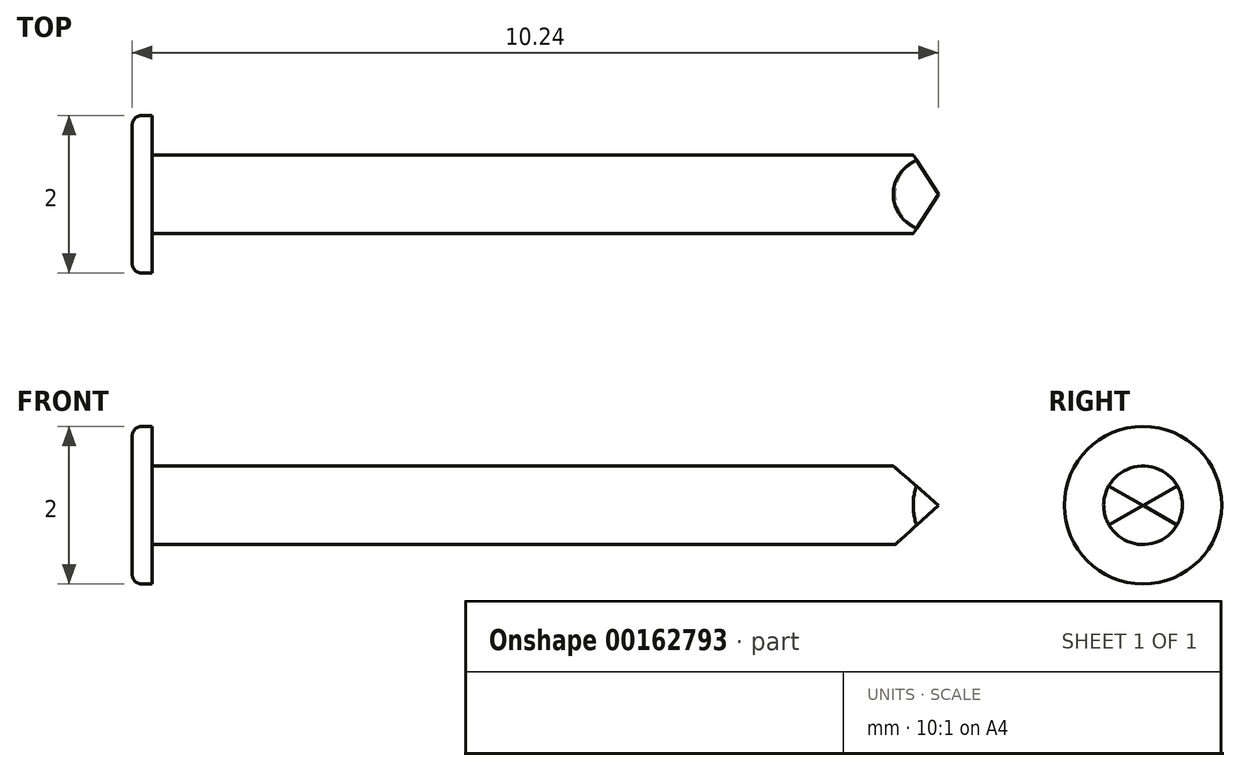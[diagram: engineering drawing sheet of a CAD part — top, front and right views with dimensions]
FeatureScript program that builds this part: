
annotation { "Feature Type Name" : "Feature", "Feature Type Description" : "" }
export const myFeature = defineFeature(function(context is Context, id is Id, definition is map)
    precondition{}
    {
        {
            var Q0;
            Q0=qCreatedBy(makeId("Right.planeOp"),FACE);
            var sketch = newSketch(context, id + "F0", { "sketchPlane" : qUnion([Q0])});
            skCircle(sketch, "E0", {"center": v(0, 0) * mm, "radius": 1 * mm});
            skCircle(sketch, "E1", {"center": v(0, 0) * mm, "radius": 0.5 * mm});
            skSolve(sketch);
        }
        {
            var Q0;
            Q0=makeQuery(id+"F0.imprint","IMPRINT",FACE,{"disambiguationData":[TD([[makeQuery(id+"F0.imprint","IMPRINT",EDGE,{"derivedFrom":sQuery(id+"F0.wireOp",EDGE,"E1")}),1.0]])]});
            var Q1;
            Q1=sQuery(id+"F0.wireOp",EDGE,"E1");
            extrude(context, id + "F1", {"entities" : qUnion([Q0]), "surfaceEntities" : qUnion([Q1]), "depth" : 10 * mm});
        }
        {
            var Q0;
            Q0=makeQuery(id+"F0.imprint","IMPRINT",FACE,{"disambiguationData":[TD([[makeQuery(id+"F0.imprint","IMPRINT",EDGE,{"derivedFrom":sQuery(id+"F0.wireOp",EDGE,"E1")}),1.0]])]});
            var Q1;
            Q1=makeQuery(id+"F0.imprint","IMPRINT",FACE,{"disambiguationData":[TD([[makeQuery(id+"F0.imprint","IMPRINT",EDGE,{"derivedFrom":sQuery(id+"F0.wireOp",EDGE,"E0")}),1.0]])]});
            var Q2;
            Q2=sQuery(id+"F0.wireOp",EDGE,"E1");
            var Q3;
            Q3=sQuery(id+"F0.wireOp",EDGE,"E0");
            extrude(context, id + "F2", {"entities" : qUnion([Q0, Q1]), "operationType" : NewBodyOperationType.ADD, "surfaceEntities" : qUnion([Q2, Q3]), "oppositeDirection" : true, "depth" : 0.25 * mm});
        }
        {
            var Q0;
            Q0=makeQuery(id+"F2.opExtrude","CAP_EDGE",EDGE,{"disambiguationData":[OSD([sQuery(id+"F0.wireOp",EDGE,"E0")])],"isStart":false});
            fillet(context, id + "F3", {"entities" : qUnion([Q0]), "radius" : 0.12 * mm, "tangentPropagation" : true, "allowEdgeOverflow" : false});
        }
        {
            var Q0;
            Q0=qCreatedBy(makeId("Front.planeOp"),FACE);
            var sketch = newSketch(context, id + "F4", { "sketchPlane" : qUnion([Q0])});
            skLineSegment(sketch, "E2", {"start": v(10, 0) * mm, "end": v(9.12, -0.8) * mm});
            skLineSegment(sketch, "E3", {"start": v(9.12, -0.8) * mm, "end": v(10.61, -1.03) * mm});
            skLineSegment(sketch, "E4", {"start": v(10.61, -1.03) * mm, "end": v(10.75, 0.92) * mm});
            skLineSegment(sketch, "E5", {"start": v(10.75, 0.92) * mm, "end": v(9, 0.86) * mm});
            skLineSegment(sketch, "E6", {"start": v(9, 0.86) * mm, "end": v(10, 0) * mm});
            skSolve(sketch);
        }
        {
            var Q0;
            Q0=makeQuery(id+"F4.imprint","IMPRINT",FACE,{"disambiguationData":[TD([[makeQuery(id+"F4.imprint","IMPRINT",EDGE,{"derivedFrom":sQuery(id+"F4.wireOp",EDGE,"E2")}),1.0]])]});
            extrude(context, id + "F5", {"entities" : qUnion([Q0]), "operationType" : NewBodyOperationType.REMOVE, "depth" : 5 * mm, "hasSecondDirection" : true, "secondDirectionOppositeDirection" : true, "secondDirectionDepth" : 5 * mm});
        }
        {
            var Q0;
            Q0=qCreatedBy(makeId("Top.planeOp"),FACE);
            var sketch = newSketch(context, id + "F6", { "sketchPlane" : qUnion([Q0])});
            skLineSegment(sketch, "E7", {"start": v(9.6, 0.61) * mm, "end": v(10, 0) * mm});
            skLineSegment(sketch, "E8", {"start": v(10, 0) * mm, "end": v(9.57, -0.65) * mm});
            skLineSegment(sketch, "E9", {"start": v(9.57, -0.65) * mm, "end": v(10.34, -0.65) * mm});
            skLineSegment(sketch, "E10", {"start": v(10.34, -0.65) * mm, "end": v(10.34, 0.61) * mm});
            skLineSegment(sketch, "E11", {"start": v(10.34, 0.61) * mm, "end": v(9.6, 0.61) * mm});
            skSolve(sketch);
        }
        {
            var Q0;
            Q0 = qSketchRegion(id + "F6", true);
            extrude(context, id + "F7", {"entities" : qUnion([Q0]), "operationType" : NewBodyOperationType.REMOVE, "depth" : 25 * mm, "hasSecondDirection" : true, "secondDirectionOppositeDirection" : true, "secondDirectionDepth" : 25 * mm});
        }
    });
